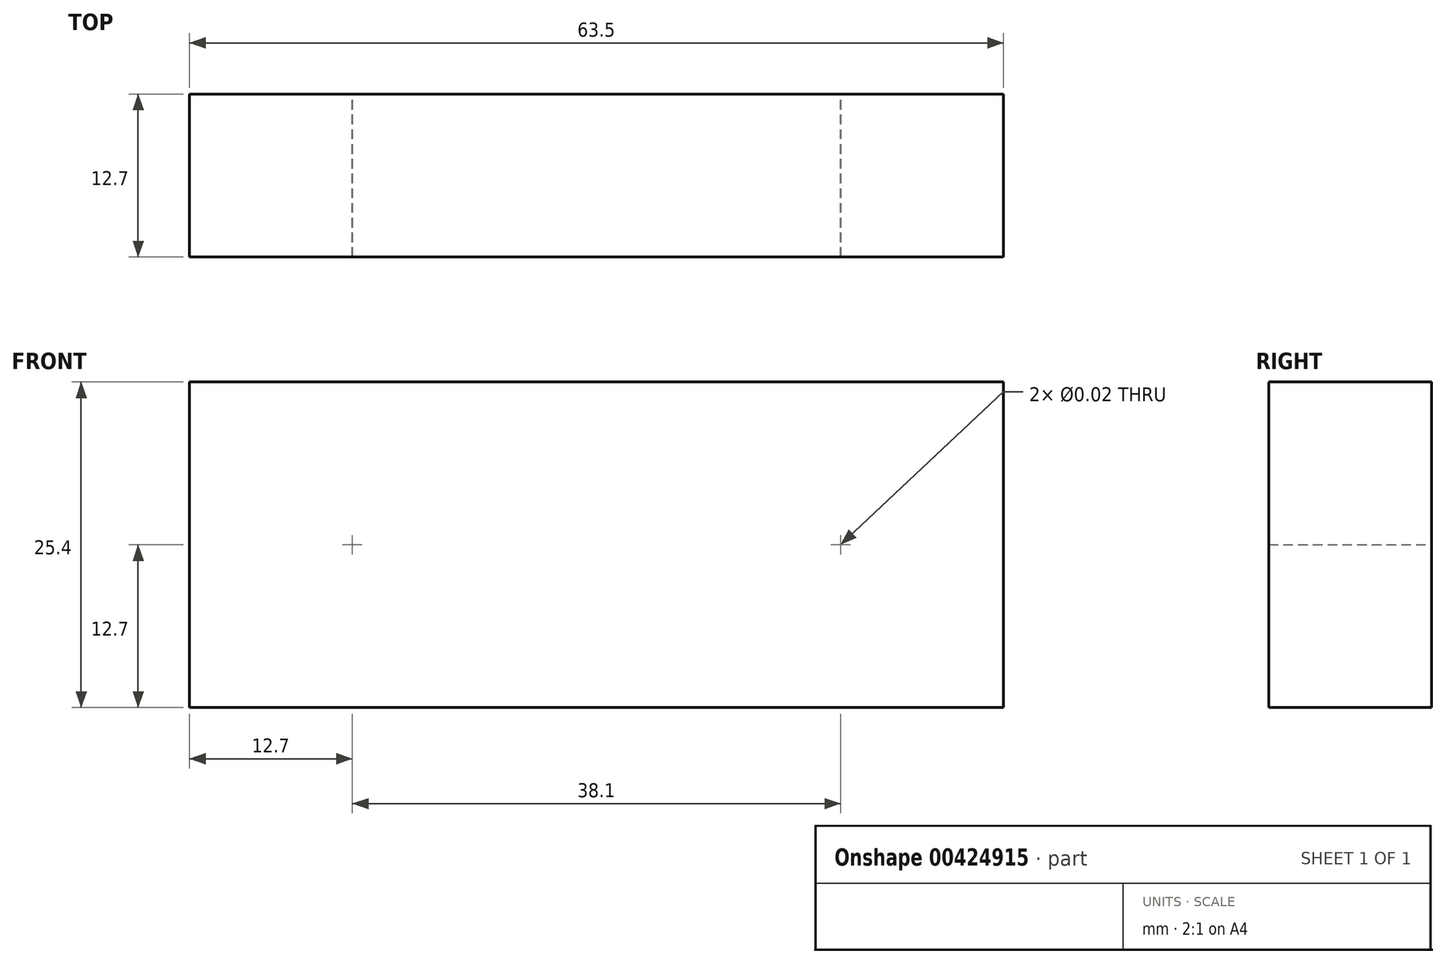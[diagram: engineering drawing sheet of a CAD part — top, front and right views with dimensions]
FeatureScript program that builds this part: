
annotation { "Feature Type Name" : "Feature", "Feature Type Description" : "" }
export const myFeature = defineFeature(function(context is Context, id is Id, definition is map)
    precondition{}
    {
        {
            var Q0;
            Q0=qCreatedBy(makeId("Front.planeOp"),FACE);
            var sketch = newSketch(context, id + "F0", { "sketchPlane" : qUnion([Q0])});
            skLineSegment(sketch, "E0.bottom", {"start": v(31.75, -12.7) * mm, "end": v(-31.75, -12.7) * mm});
            skLineSegment(sketch, "E0.top", {"start": v(31.75, 12.7) * mm, "end": v(-31.75, 12.7) * mm});
            skLineSegment(sketch, "E0.left", {"start": v(31.75, -12.7) * mm, "end": v(31.75, 12.7) * mm});
            skLineSegment(sketch, "E0.right", {"start": v(-31.75, -12.7) * mm, "end": v(-31.75, 12.7) * mm});
            skPoint(sketch, "E0.middle", {"position": v(0, 0) * mm});
            skSolve(sketch);
        }
        {
            var Q0;
            Q0 = qSketchRegion(id + "F0", true);
            extrude(context, id + "F1", {"entities" : qUnion([Q0]), "depth" : 12.7 * mm});
        }
        {
            var Q0;
            Q0=makeQuery(id+"F1.opExtrude","CAP_FACE",FACE,{"disambiguationData":[OSD([sQuery(id+"F0.wireOp",EDGE,"E0.bottom"),sQuery(id+"F0.wireOp",EDGE,"E0.top"),sQuery(id+"F0.wireOp",EDGE,"E0.left"),sQuery(id+"F0.wireOp",EDGE,"E0.right")])],"isStart":false});
            var sketch = newSketch(context, id + "F2", { "sketchPlane" : qUnion([Q0])});
            skLineSegment(sketch, "E1", {"start": v(31.75, 0) * mm, "end": v(-31.75, 0) * mm, "construction": true});
            skPoint(sketch, "E2", {"position": v(-19.05, 0) * mm});
            skPoint(sketch, "E3", {"position": v(19.05, 0) * mm});
            skSolve(sketch);
        }
        {
            var Q0;
            Q0=sQuery(id+"F2.wireOp",VERTEX,"E2");
            var Q1;
            Q1=sQuery(id+"F2.wireOp",VERTEX,"E3");
            var Q2;
            Q2=makeQuery(id+"F1.opExtrude","SWEPT_BODY",BODY,{"disambiguationData":[OSD([sQuery(id+"F0.wireOp",EDGE,"E0.bottom"),sQuery(id+"F0.wireOp",EDGE,"E0.top"),sQuery(id+"F0.wireOp",EDGE,"E0.left"),sQuery(id+"F0.wireOp",EDGE,"E0.right")])]});
            hole(context, id + "F3", {"style" : HoleStyle.SIMPLE, "endStyle" : HoleEndStyle.THROUGH, "standardTappedOrClearance" : lookupTablePath({ "standard" : "ANSI", "size" : "1/2 (0.5)", "type" : "Drilled" }), "standardBlindInLast" : lookupTablePath({ "standard" : "ANSI", "size" : "1/2", "type" : "Drilled" }), "holeDiameter" : 1 / 50.8 * mm, "isTappedThrough" : true, "tappedDepth" : 10.3 * mm, "tapClearance" : 3, "locations" : qUnion([Q0, Q1]), "scope" : qUnion([Q2]), "startStyle" : HoleStartStyle.SKETCH});
        }
    });
